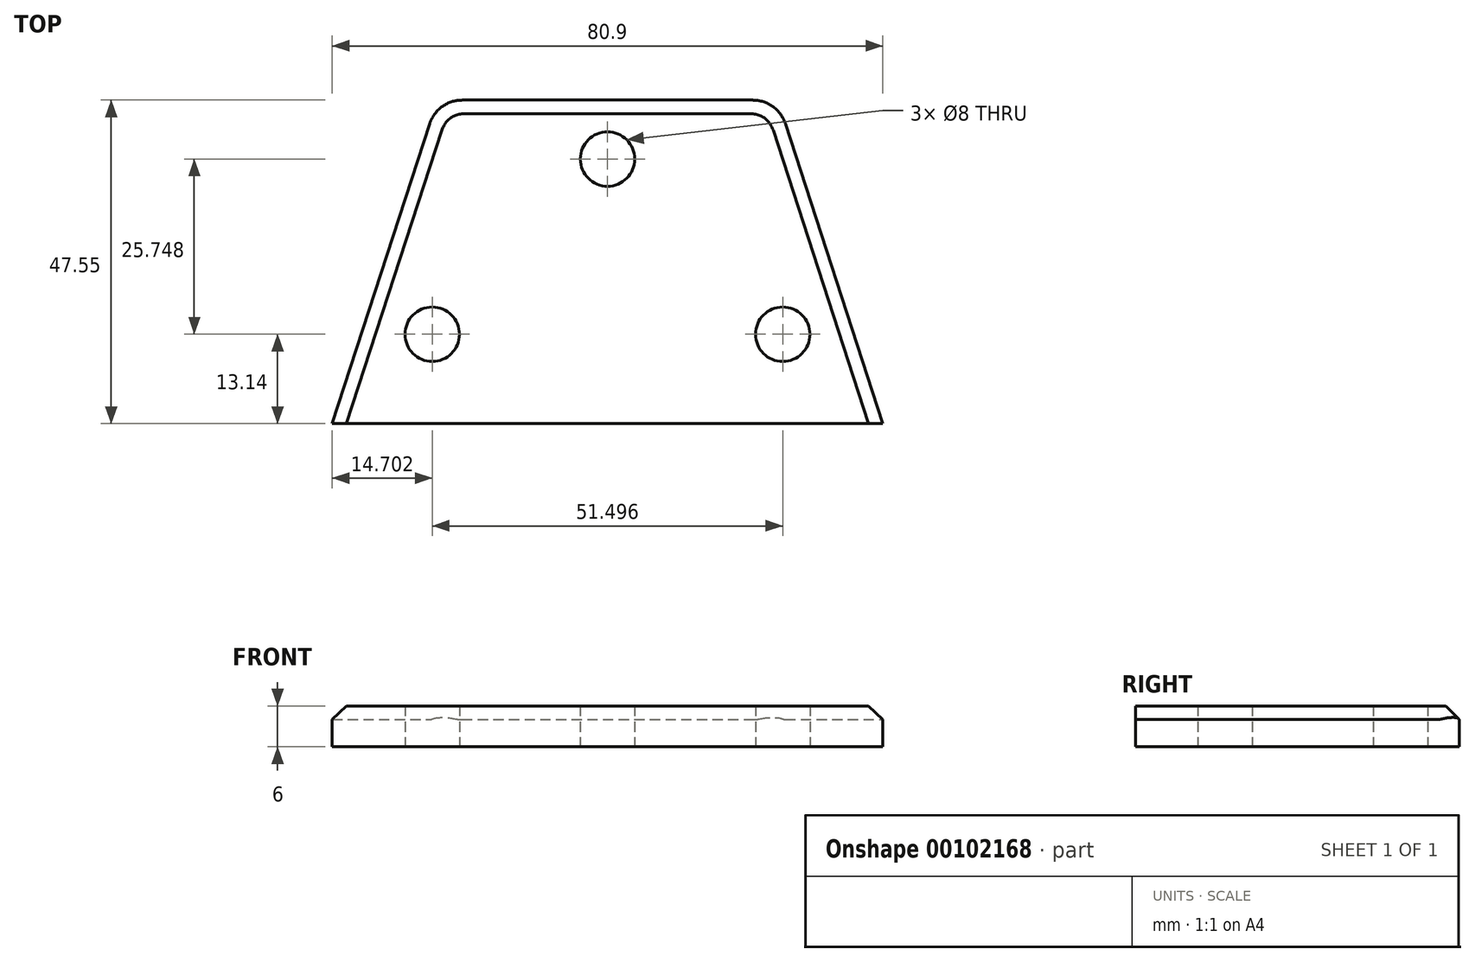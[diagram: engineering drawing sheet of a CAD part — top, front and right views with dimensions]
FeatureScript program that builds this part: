
annotation { "Feature Type Name" : "Feature", "Feature Type Description" : "" }
export const myFeature = defineFeature(function(context is Context, id is Id, definition is map)
    precondition{}
    {
        {
            var Q0;
            Q0=qCreatedBy(makeId("Top.planeOp"),FACE);
            var sketch = newSketch(context, id + "F0", { "sketchPlane" : qUnion([Q0])});
            skArc(sketch, "E0.cCircle", {"start": v(31.8, -13.14) * mm, "mid": v(0, 34.4) * mm, "end": v(-31.8, -13.14) * mm, "construction": true});
            skLineSegment(sketch, "E0.0", {"start": v(25, 34.4) * mm, "end": v(40.45, -13.14) * mm});
            skLineSegment(sketch, "E0.3", {"start": v(-40.45, -13.14) * mm, "end": v(-25, 34.4) * mm});
            skLineSegment(sketch, "E0.4", {"start": v(-25, 34.4) * mm, "end": v(25, 34.4) * mm});
            skPoint(sketch, "E0.0.midPoint", {"position": v(32.73, 10.63) * mm});
            skLineSegment(sketch, "E1", {"start": v(-40.45, -13.14) * mm, "end": v(40.45, -13.14) * mm});
            skCircle(sketch, "E2", {"center": v(0, 25.75) * mm, "radius": 4 * mm});
            skCircle(sketch, "E3.1.0", {"center": v(-25.75, 0) * mm, "radius": 4 * mm});
            skCircle(sketch, "E4.1.3.0", {"center": v(25.75, 0) * mm, "radius": 4 * mm});
            skSolve(sketch);
        }
        {
            var Q0;
            Q0=makeQuery(id+"F0.imprint","IMPRINT",FACE,{"disambiguationData":[TD([[makeQuery(id+"F0.imprint","IMPRINT",EDGE,{"derivedFrom":sQuery(id+"F0.wireOp",EDGE,"E0.0")}),-1.0]])]});
            extrude(context, id + "F1", {"entities" : qUnion([Q0]), "depth" : 6 * mm});
        }
        {
            var Q0;
            Q0=makeQuery(id+"F1.opExtrude","CAP_EDGE",EDGE,{"disambiguationData":[OSD([sQuery(id+"F0.wireOp",EDGE,"E0.4")])],"isStart":false});
            var Q1;
            Q1=makeQuery(id+"F1.opExtrude","CAP_EDGE",EDGE,{"disambiguationData":[OSD([sQuery(id+"F0.wireOp",EDGE,"E0.0")])],"isStart":false});
            var Q2;
            Q2=makeQuery(id+"F1.opExtrude","CAP_EDGE",EDGE,{"disambiguationData":[OSD([sQuery(id+"F0.wireOp",EDGE,"E0.3")])],"isStart":false});
            chamfer(context, id + "F2", {"entities" : qUnion([Q0, Q1, Q2]), "width" : 2 * mm, "tangentPropagation" : true});
        }
        {
            var Q0;
            Q0=makeQuery(id+"F1.opExtrude","SWEPT_EDGE",EDGE,{"disambiguationData":[OSD([sQuery(id+"F0.wireOp",EDGE,"E0.3"),sQuery(id+"F0.wireOp",EDGE,"E0.4")])]});
            var Q1;
            Q1=makeQuery(id+"F2.opChamfer","BLEND_EDGE",EDGE,{"blendedFrom":[makeQuery(id+"F1.opExtrude","CAP_EDGE",EDGE,{"disambiguationData":[OSD([sQuery(id+"F0.wireOp",EDGE,"E0.3")])],"isStart":false}),makeQuery(id+"F1.opExtrude","CAP_EDGE",EDGE,{"disambiguationData":[OSD([sQuery(id+"F0.wireOp",EDGE,"E0.4")])],"isStart":false})],"blendedInto":[]});
            var Q2;
            Q2=makeQuery(id+"F1.opExtrude","SWEPT_EDGE",EDGE,{"disambiguationData":[OSD([sQuery(id+"F0.wireOp",EDGE,"E0.0"),sQuery(id+"F0.wireOp",EDGE,"E0.4")])]});
            var Q3;
            Q3=makeQuery(id+"F2.opChamfer","BLEND_EDGE",EDGE,{"blendedFrom":[makeQuery(id+"F1.opExtrude","CAP_EDGE",EDGE,{"disambiguationData":[OSD([sQuery(id+"F0.wireOp",EDGE,"E0.0")])],"isStart":false}),makeQuery(id+"F1.opExtrude","CAP_EDGE",EDGE,{"disambiguationData":[OSD([sQuery(id+"F0.wireOp",EDGE,"E0.4")])],"isStart":false})],"blendedInto":[]});
            fillet(context, id + "F3", {"entities" : qUnion([Q0, Q1, Q2, Q3]), "radius" : 5 * mm, "tangentPropagation" : true, "allowEdgeOverflow" : false});
        }
    });
